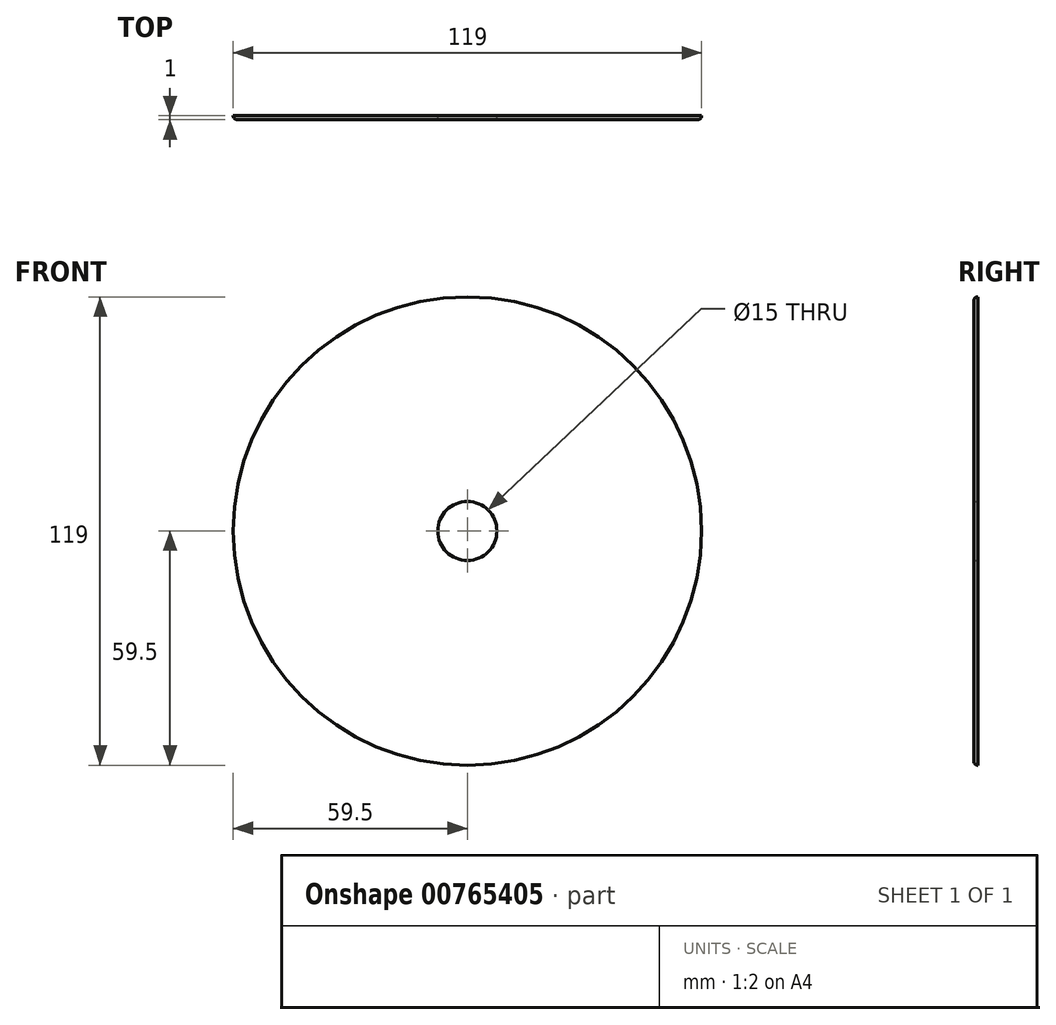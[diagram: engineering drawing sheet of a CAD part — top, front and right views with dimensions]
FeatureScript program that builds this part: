
annotation { "Feature Type Name" : "Feature", "Feature Type Description" : "" }
export const myFeature = defineFeature(function(context is Context, id is Id, definition is map)
    precondition{}
    {
        {
            var Q0;
            Q0=qCreatedBy(makeId("Front.planeOp"),FACE);
            var sketch = newSketch(context, id + "F0", { "sketchPlane" : qUnion([Q0])});
            skCircle(sketch, "E0", {"center": v(0, 0) * mm, "radius": 59.5 * mm});
            skCircle(sketch, "E1", {"center": v(0, 0) * mm, "radius": 7.5 * mm});
            skSolve(sketch);
        }
        {
            var Q0;
            Q0 = qSketchRegion(id + "F0", true);
            extrude(context, id + "F1", {"entities" : qUnion([Q0]), "depth" : 1 * mm, "offsetDistance" : 25 * mm});
        }
        {
            var Q0;
            Q0=makeQuery(id+"F1.opExtrude","CAP_EDGE",EDGE,{"disambiguationData":[OSD([sQuery(id+"F0.wireOp",EDGE,"E0")])],"isStart":false});
            fillet(context, id + "F2", {"entities" : qUnion([Q0]), "radius" : 1 * mm, "tangentPropagation" : true, "allowEdgeOverflow" : false});
        }
    });
